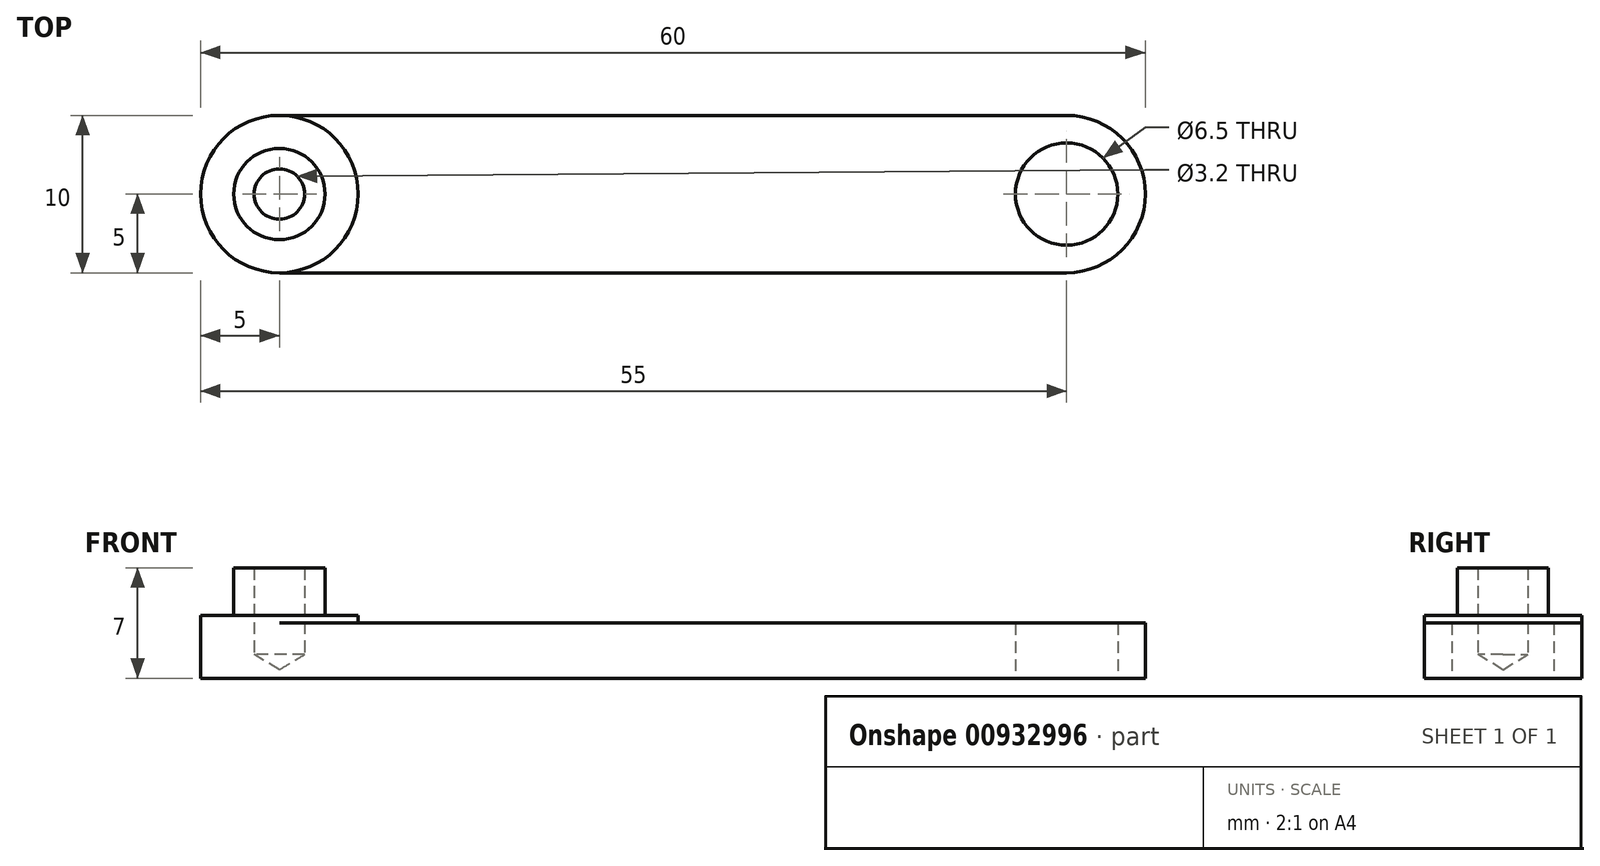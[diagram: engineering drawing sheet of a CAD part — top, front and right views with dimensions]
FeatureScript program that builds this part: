
annotation { "Feature Type Name" : "Feature", "Feature Type Description" : "" }
export const myFeature = defineFeature(function(context is Context, id is Id, definition is map)
    precondition{}
    {
        {
            var Q0;
            Q0=qCreatedBy(makeId("Top.planeOp"),FACE);
            var sketch = newSketch(context, id + "F0", { "sketchPlane" : qUnion([Q0])});
            skLineSegment(sketch, "E0.bottom", {"start": v(25, -5) * mm, "end": v(-25, -5) * mm});
            skLineSegment(sketch, "E0.top", {"start": v(25, 5) * mm, "end": v(-25, 5) * mm});
            skLineSegment(sketch, "E0.left", {"start": v(25, -5) * mm, "end": v(25, 5) * mm});
            skLineSegment(sketch, "E0.right", {"start": v(-25, -5) * mm, "end": v(-25, 5) * mm});
            skPoint(sketch, "E0.middle", {"position": v(0, 0) * mm});
            skArc(sketch, "E1", {"start": v(25, -5) * mm, "mid": v(30, 0) * mm, "end": v(25, 5) * mm});
            skArc(sketch, "E2", {"start": v(-25, 5) * mm, "mid": v(-30, 0) * mm, "end": v(-25, -5) * mm});
            skCircle(sketch, "E3", {"center": v(25, 0) * mm, "radius": 3.25 * mm});
            skSolve(sketch);
        }
        {
            var Q0;
            {var subQ5=sQuery(id+"F0.wireOp",EDGE,"E0.bottom");Q0=makeQuery(id+"F0.imprint","IMPRINT",FACE,{"disambiguationData":[TD([[makeQuery(id+"F0.imprint","IMPRINT",EDGE,{"derivedFrom":subQ5}),-1.0]])]});}
            var Q1;
            {var subQ0=sQuery(id+"F0.wireOp",EDGE,"E2");Q1=makeQuery(id+"F0.imprint","IMPRINT",FACE,{"disambiguationData":[TD([[makeQuery(id+"F0.imprint","IMPRINT",EDGE,{"derivedFrom":subQ0}),1.0]])]});}
            var Q2;
            {var subQ0=sQuery(id+"F0.wireOp",EDGE,"E1");Q2=makeQuery(id+"F0.imprint","IMPRINT",FACE,{"disambiguationData":[TD([[makeQuery(id+"F0.imprint","IMPRINT",EDGE,{"derivedFrom":subQ0}),1.0]])]});}
            extrude(context, id + "F1", {"entities" : qUnion([Q0, Q1, Q2]), "depth" : 3.5 * mm, "offsetDistance" : 25 * mm});
        }
        {
            var Q0;
            Q0=makeQuery(id+"F1.opExtrude","CAP_FACE",FACE,{"disambiguationData":[OSD([sQuery(id+"F0.wireOp",EDGE,"E0.bottom"),sQuery(id+"F0.wireOp",EDGE,"E0.top"),sQuery(id+"F0.wireOp",EDGE,"E1"),sQuery(id+"F0.wireOp",EDGE,"E2"),sQuery(id+"F0.wireOp",EDGE,"NiPrGvlA-nl9o-toRk-AStp-YR2R7amF9Vjg"),sQuery(id+"F0.wireOp",EDGE,"E3")])],"isStart":false});
            var sketch = newSketch(context, id + "F2", { "sketchPlane" : qUnion([Q0])});
            skCircle(sketch, "E4", {"center": v(-25, 0) * mm, "radius": 5 * mm});
            skSolve(sketch);
        }
        {
            var Q0;
            {var subQ0=sQuery(id+"F2.wireOp",EDGE,"E4");var subQ1=makeQuery(id+"F2.imprint","INTERSECT",VERTEX,{"derivedFrom":[makeQuery(id+"F1.opExtrude","CAP_EDGE",EDGE,{"disambiguationData":[OSD([sQuery(id+"F0.wireOp",EDGE,"E0.bottom")])],"isStart":false}),subQ0]});Q0=makeQuery(id+"F2.imprint","IMPRINT",FACE,{"disambiguationData":[TD([[makeQuery(id+"F2.imprint","IMPRINT",EDGE,{"disambiguationData":[TD([[subQ1,1.0]])],"derivedFrom":subQ0}),1.0]])]});}
            extrude(context, id + "F3", {"entities" : qUnion([Q0]), "operationType" : NewBodyOperationType.ADD, "depth" : 0.5 * mm, "offsetDistance" : 25 * mm});
        }
        {
            var Q0;
            Q0=makeQuery(id+"F3.opExtrude","CAP_FACE",FACE,{"disambiguationData":[OSD([sQuery(id+"F2.wireOp",EDGE,"E4")])],"isStart":false});
            var sketch = newSketch(context, id + "F4", { "sketchPlane" : qUnion([Q0])});
            skPoint(sketch, "E5", {"position": v(-25, 0) * mm});
            skCircle(sketch, "E6", {"center": v(-25, 0) * mm, "radius": 3 * mm});
            skSolve(sketch);
        }
        {
            var Q0;
            Q0=sQuery(id+"F4.wireOp",VERTEX,"E5");
            var Q1;
            Q1=makeQuery(id+"F1.opExtrude","SWEPT_BODY",BODY,{"disambiguationData":[OSD([sQuery(id+"F0.wireOp",EDGE,"E0.bottom"),sQuery(id+"F0.wireOp",EDGE,"E0.top"),sQuery(id+"F0.wireOp",EDGE,"E1"),sQuery(id+"F0.wireOp",EDGE,"E2"),sQuery(id+"F0.wireOp",EDGE,"E3")])]});
            hole(context, id + "F5", {"style" : HoleStyle.SIMPLE, "endStyle" : HoleEndStyle.BLIND, "holeDiameter" : 3.2 * mm, "majorDiameter" : 5 * mm, "holeDepth" : 2.5 * mm, "isTappedThrough" : true, "tappedDepth" : 12 * mm, "tapClearance" : 3, "locations" : qUnion([Q0]), "scope" : qUnion([Q1]), "startStyle" : HoleStartStyle.PART});
        }
        {
            var Q0;
            Q0=makeQuery(id+"F3.opExtrude","CAP_FACE",FACE,{"disambiguationData":[OSD([sQuery(id+"F2.wireOp",EDGE,"E4")])],"isStart":false});
            var sketch = newSketch(context, id + "F6", { "sketchPlane" : qUnion([Q0])});
            skCircle(sketch, "E7", {"center": v(-25, 0) * mm, "radius": 2.9 * mm});
            skSolve(sketch);
        }
        {
            var Q0;
            Q0=makeQuery(id+"F6.imprint","IMPRINT",FACE,{"disambiguationData":[TD([[makeQuery(id+"F6.imprint","IMPRINT",EDGE,{"derivedFrom":sQuery(id+"F6.wireOp",EDGE,"E7")}),1.0]])]});
            extrude(context, id + "F7", {"entities" : qUnion([Q0]), "operationType" : NewBodyOperationType.ADD, "depth" : 3 * mm, "offsetDistance" : 25 * mm});
        }
    });
